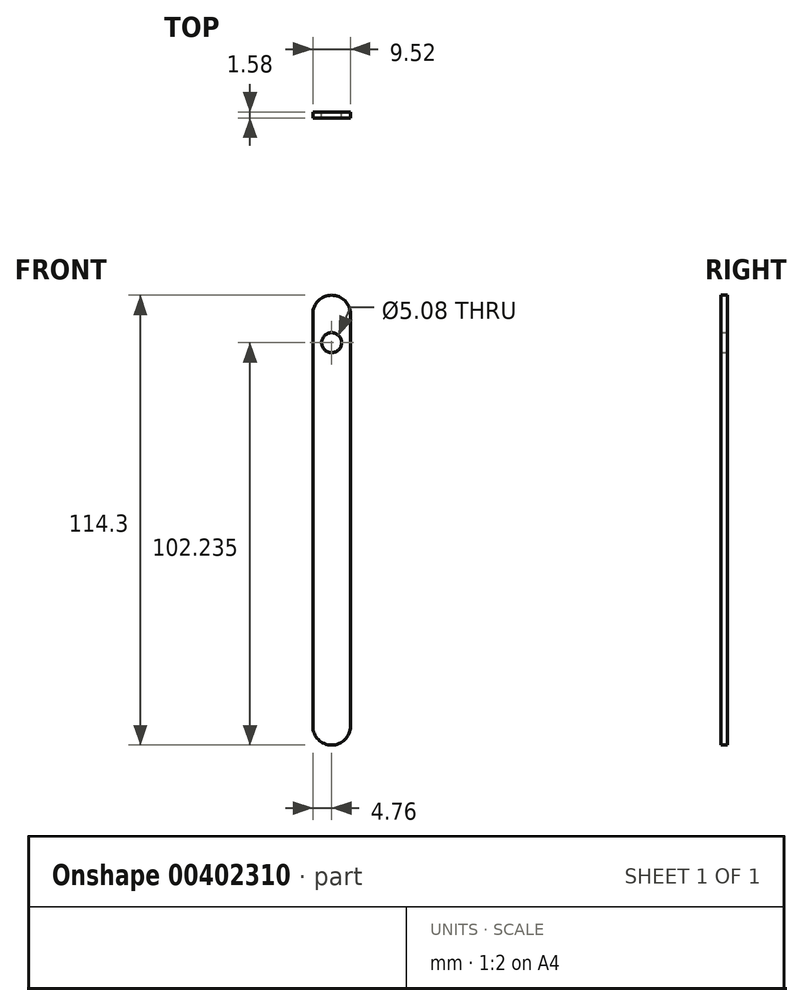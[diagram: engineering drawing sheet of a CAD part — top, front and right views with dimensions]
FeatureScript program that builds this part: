
annotation { "Feature Type Name" : "Feature", "Feature Type Description" : "" }
export const myFeature = defineFeature(function(context is Context, id is Id, definition is map)
    precondition{}
    {
        {
            var Q0;
            Q0=qCreatedBy(makeId("Front.planeOp"),FACE);
            var sketch = newSketch(context, id + "F0", { "sketchPlane" : qUnion([Q0])});
            skLineSegment(sketch, "E0.bottom", {"start": v(-4.76, 52.39) * mm, "end": v(4.76, 52.39) * mm});
            skLineSegment(sketch, "E0.top", {"start": v(-4.76, -52.39) * mm, "end": v(4.76, -52.39) * mm});
            skLineSegment(sketch, "E0.left", {"start": v(-4.76, 52.39) * mm, "end": v(-4.76, -52.39) * mm});
            skLineSegment(sketch, "E0.right", {"start": v(4.76, 52.39) * mm, "end": v(4.76, -52.39) * mm});
            skPoint(sketch, "E0.middle", {"position": v(0, 0) * mm});
            skArc(sketch, "E1", {"start": v(-4.76, 52.39) * mm, "mid": v(0, 57.15) * mm, "end": v(4.76, 52.39) * mm});
            skArc(sketch, "E2", {"start": v(-4.76, -52.39) * mm, "mid": v(0, -57.15) * mm, "end": v(4.76, -52.39) * mm});
            skSolve(sketch);
        }
        {
            var Q0;
            Q0 = qSketchRegion(id + "F0", true);
            extrude(context, id + "F1", {"entities" : qUnion([Q0]), "depth" : 1.59 * mm, "symmetric" : true});
        }
        {
            var Q0;
            Q0=makeQuery(id+"F1.opExtrude","CAP_FACE",FACE,{"disambiguationData":[OSD([sQuery(id+"F0.wireOp",EDGE,"E0.left"),sQuery(id+"F0.wireOp",EDGE,"E0.right"),sQuery(id+"F0.wireOp",EDGE,"E1"),sQuery(id+"F0.wireOp",EDGE,"E2")])],"isStart":true});
            var sketch = newSketch(context, id + "F2", { "sketchPlane" : qUnion([Q0])});
            skCircle(sketch, "E3", {"center": v(0, 45.09) * mm, "radius": 2.54 * mm});
            skSolve(sketch);
        }
        {
            var Q0;
            Q0 = qSketchRegion(id + "F2", true);
            extrude(context, id + "F3", {"entities" : qUnion([Q0]), "operationType" : NewBodyOperationType.REMOVE, "endBound" : BoundingType.UP_TO_NEXT, "oppositeDirection" : true, "depth" : 10.4 * mm});
        }
    });
